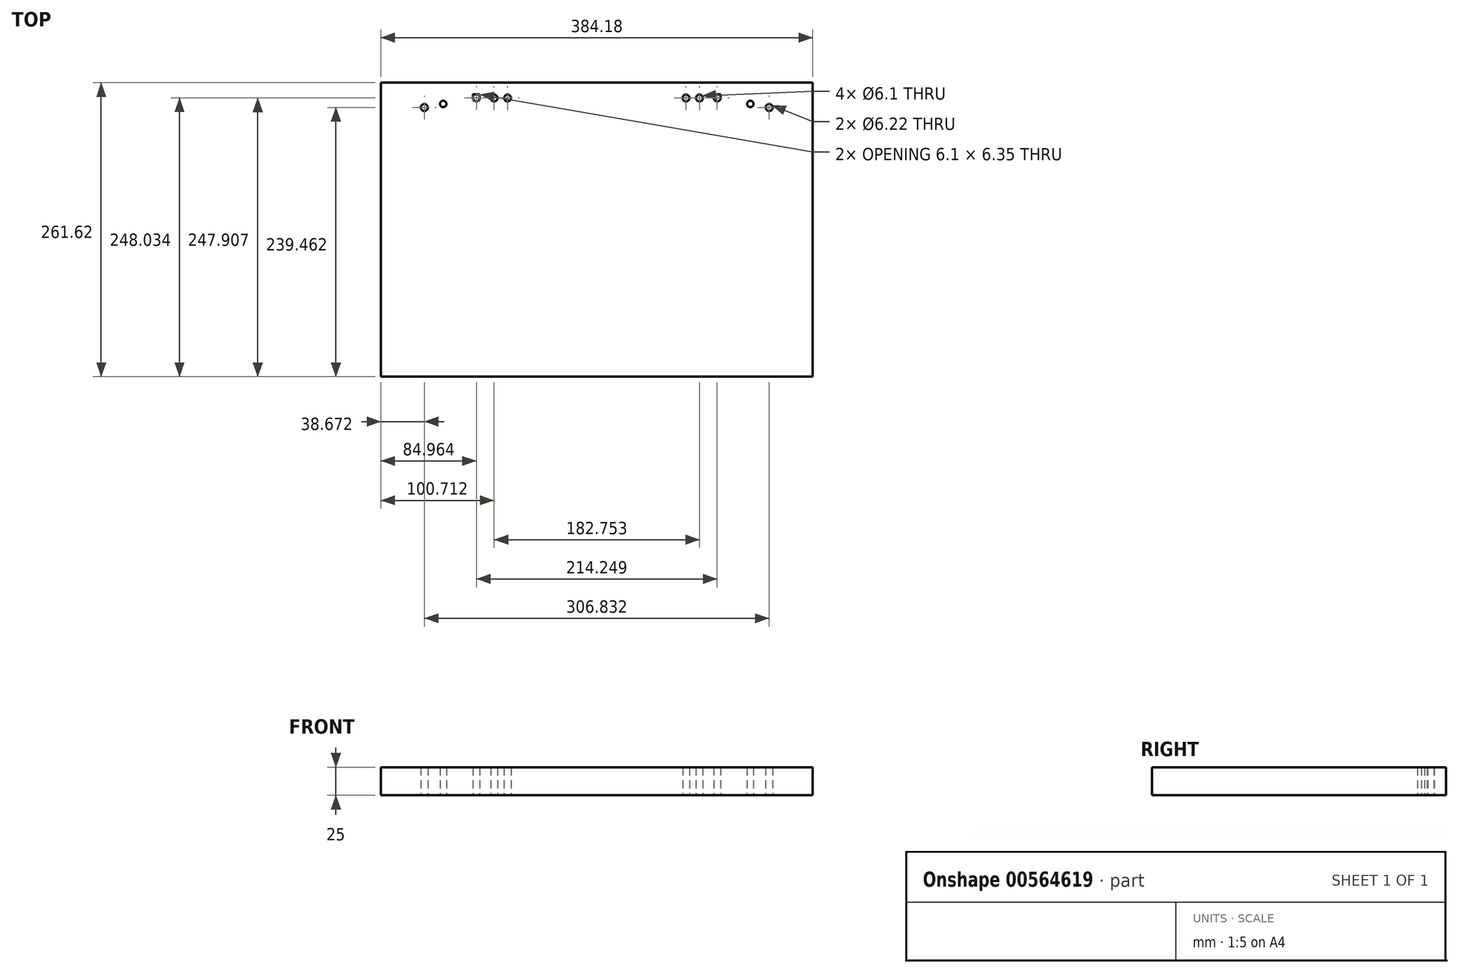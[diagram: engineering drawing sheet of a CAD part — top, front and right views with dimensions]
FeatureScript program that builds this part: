
annotation { "Feature Type Name" : "Feature", "Feature Type Description" : "" }
export const myFeature = defineFeature(function(context is Context, id is Id, definition is map)
    precondition{}
    {
        {
            var Q0;
            Q0=qCreatedBy(makeId("Top.planeOp"),FACE);
            var sketch = newSketch(context, id + "F0", { "sketchPlane" : qUnion([Q0])});
            skLineSegment(sketch, "E0.bottom", {"start": v(-193.7, 115.56) * mm, "end": v(190.47, 115.56) * mm});
            skLineSegment(sketch, "E0.top", {"start": v(-193.7, -146.06) * mm, "end": v(190.47, -146.06) * mm});
            skLineSegment(sketch, "E0.left", {"start": v(-193.7, 115.56) * mm, "end": v(-193.7, -146.06) * mm});
            skLineSegment(sketch, "E0.right", {"start": v(190.47, 115.56) * mm, "end": v(190.47, -146.06) * mm});
            skLineSegment(sketch, "E1", {"start": v(144.25, -146.06) * mm, "end": v(144.25, 88.39) * mm, "construction": true});
            skLineSegment(sketch, "E2", {"start": v(72.23, 88.39) * mm, "end": v(156.3, 88.39) * mm});
            skLineSegment(sketch, "E3", {"start": v(156.3, 88.39) * mm, "end": v(156.3, 100.96) * mm});
            skLineSegment(sketch, "E4", {"start": v(156.3, 94.67) * mm, "end": v(190.47, 94.67) * mm, "construction": true});
            skLineSegment(sketch, "E5", {"start": v(151.8, -146.06) * mm, "end": v(151.8, 90.3) * mm, "construction": true});
            skLineSegment(sketch, "E6", {"start": v(190.47, 93.4) * mm, "end": v(154.9, 93.4) * mm, "construction": true});
            skCircle(sketch, "E7", {"center": v(151.8, 93.4) * mm, "radius": 3.11 * mm});
            skLineSegment(sketch, "E8", {"start": v(151.8, 90.3) * mm, "end": v(151.8, 93.4) * mm, "construction": true});
            skLineSegment(sketch, "E9", {"start": v(154.9, 93.4) * mm, "end": v(151.8, 93.4) * mm, "construction": true});
            skLineSegment(sketch, "E10", {"start": v(135.03, -146.06) * mm, "end": v(135.03, 93.72) * mm, "construction": true});
            skLineSegment(sketch, "E11", {"start": v(190.47, 96.58) * mm, "end": v(137.89, 96.58) * mm, "construction": true});
            skCircle(sketch, "E12", {"center": v(135.03, 96.58) * mm, "radius": 2.86 * mm});
            skLineSegment(sketch, "E13", {"start": v(135.03, 96.58) * mm, "end": v(137.89, 96.58) * mm, "construction": true});
            skLineSegment(sketch, "E14", {"start": v(135.03, 96.58) * mm, "end": v(135.03, 93.72) * mm, "construction": true});
            skLineSegment(sketch, "E15", {"start": v(190.47, 101.85) * mm, "end": v(108.55, 101.85) * mm, "construction": true});
            skLineSegment(sketch, "E16", {"start": v(105.5, -146.06) * mm, "end": v(105.5, 98.8) * mm, "construction": true});
            skLineSegment(sketch, "E17", {"start": v(105.5, 101.85) * mm, "end": v(108.55, 101.85) * mm, "construction": true});
            skLineSegment(sketch, "E18", {"start": v(105.5, 101.85) * mm, "end": v(105.5, 98.8) * mm, "construction": true});
            skLineSegment(sketch, "E19", {"start": v(105.5, 101.85) * mm, "end": v(102.45, 101.85) * mm, "construction": true});
            skLineSegment(sketch, "E20", {"start": v(102.45, 101.85) * mm, "end": v(102.45, 101.85) * mm});
            skLineSegment(sketch, "E21", {"start": v(108.55, 101.85) * mm, "end": v(108.55, 101.85) * mm});
            skArc(sketch, "E22", {"start": v(102.45, 101.85) * mm, "mid": v(105.5, 98.8) * mm, "end": v(108.55, 101.85) * mm});
            skLineSegment(sketch, "E23", {"start": v(102.45, 101.85) * mm, "end": v(102.45, 105.15) * mm});
            skLineSegment(sketch, "E24", {"start": v(102.45, 105.15) * mm, "end": v(108.55, 105.15) * mm});
            skLineSegment(sketch, "E25", {"start": v(108.55, 105.15) * mm, "end": v(108.55, 101.85) * mm});
            skLineSegment(sketch, "E26", {"start": v(102.45, 101.85) * mm, "end": v(92.8, 101.85) * mm, "construction": true});
            skCircle(sketch, "E27", {"center": v(89.75, 101.85) * mm, "radius": 3.05 * mm});
            skLineSegment(sketch, "E28", {"start": v(86.7, 101.85) * mm, "end": v(80.81, 101.85) * mm, "construction": true});
            skCircle(sketch, "E29", {"center": v(77.77, 101.85) * mm, "radius": 3.05 * mm});
            skLineSegment(sketch, "E30", {"start": v(72.23, 88.39) * mm, "end": v(72.23, 107.44) * mm});
            skLineSegment(sketch, "E31", {"start": v(72.23, 107.44) * mm, "end": v(156.3, 107.44) * mm});
            skLineSegment(sketch, "E32", {"start": v(156.3, 107.44) * mm, "end": v(156.3, 100.96) * mm});
            skLineSegment(sketch, "E33", {"start": v(-1.62, 115.56) * mm, "end": v(-1.62, -146.06) * mm});
            skLineSegment(sketch, "E34.MirrorCS", {"start": v(-75.47, 107.44) * mm, "end": v(-159.55, 107.44) * mm});
            skLineSegment(sketch, "E35.MirrorCS", {"start": v(-105.7, 101.85) * mm, "end": v(-105.7, 105.15) * mm});
            skLineSegment(sketch, "E36.MirrorCS", {"start": v(-108.75, 101.85) * mm, "end": v(-111.8, 101.85) * mm, "construction": true});
            skLineSegment(sketch, "E37.MirrorCS", {"start": v(-108.75, 101.85) * mm, "end": v(-105.7, 101.85) * mm, "construction": true});
            skLineSegment(sketch, "E38.MirrorCS", {"start": v(-138.27, 96.58) * mm, "end": v(-141.13, 96.58) * mm, "construction": true});
            skLineSegment(sketch, "E39.MirrorCS", {"start": v(-108.75, 101.85) * mm, "end": v(-108.75, 98.8) * mm, "construction": true});
            skLineSegment(sketch, "E40.MirrorCS", {"start": v(-155.04, 90.3) * mm, "end": v(-155.04, 93.4) * mm, "construction": true});
            skCircle(sketch, "E41.MirrorC", {"center": v(-81, 101.85) * mm, "radius": 3.05 * mm});
            skCircle(sketch, "E42.MirrorC", {"center": v(-138.27, 96.58) * mm, "radius": 2.86 * mm});
            skLineSegment(sketch, "E43.MirrorCS", {"start": v(-159.55, 107.44) * mm, "end": v(-159.55, 100.96) * mm});
            skLineSegment(sketch, "E44.MirrorCS", {"start": v(-75.47, 88.39) * mm, "end": v(-75.47, 107.44) * mm});
            skArc(sketch, "E45.MirrorCS", {"start": v(-105.7, 101.85) * mm, "mid": v(-108.75, 98.8) * mm, "end": v(-111.8, 101.85) * mm});
            skLineSegment(sketch, "E46.MirrorCS", {"start": v(-159.55, 88.39) * mm, "end": v(-159.55, 100.96) * mm});
            skLineSegment(sketch, "E47.MirrorCS", {"start": v(-105.7, 101.85) * mm, "end": v(-105.7, 101.85) * mm});
            skLineSegment(sketch, "E48.MirrorCS", {"start": v(-158.15, 93.4) * mm, "end": v(-155.04, 93.4) * mm, "construction": true});
            skCircle(sketch, "E49.MirrorC", {"center": v(-155.04, 93.4) * mm, "radius": 3.11 * mm});
            skLineSegment(sketch, "E50.MirrorCS", {"start": v(-111.8, 105.15) * mm, "end": v(-111.8, 101.85) * mm});
            skLineSegment(sketch, "E51.MirrorCS", {"start": v(-75.47, 88.39) * mm, "end": v(-159.55, 88.39) * mm});
            skLineSegment(sketch, "E52.MirrorCS", {"start": v(-105.7, 105.15) * mm, "end": v(-111.8, 105.15) * mm});
            skLineSegment(sketch, "E53.MirrorCS", {"start": v(-111.8, 101.85) * mm, "end": v(-111.8, 101.85) * mm});
            skCircle(sketch, "E54.MirrorC", {"center": v(-93, 101.85) * mm, "radius": 3.05 * mm});
            skLineSegment(sketch, "E55.MirrorCS", {"start": v(-138.27, 96.58) * mm, "end": v(-138.27, 93.72) * mm, "construction": true});
            skSolve(sketch);
        }
        {
            var Q0;
            Q0=makeQuery(id+"F0.imprint","IMPRINT",FACE,{"disambiguationData":[TD([[makeQuery(id+"F0.imprint","IMPRINT",EDGE,{"derivedFrom":sQuery(id+"F0.wireOp",EDGE,"E2")}),1.0]])]});
            var Q1;
            Q1=makeQuery(id+"F0.imprint","IMPRINT",FACE,{"disambiguationData":[TD([[makeQuery(id+"F0.imprint","IMPRINT",EDGE,{"derivedFrom":sQuery(id+"F0.wireOp",EDGE,"E35.MirrorCS")}),-1.0]])]});
            var Q2;
            {var subQ1=sQuery(id+"F0.wireOp",EDGE,"E0.left");Q2=makeQuery(id+"F0.imprint","IMPRINT",FACE,{"disambiguationData":[TD([[makeQuery(id+"F0.imprint","IMPRINT",EDGE,{"derivedFrom":subQ1}),1.0]])]});}
            var Q3;
            {var subQ0=sQuery(id+"F0.wireOp",EDGE,"E0.right");Q3=makeQuery(id+"F0.imprint","IMPRINT",FACE,{"disambiguationData":[TD([[makeQuery(id+"F0.imprint","IMPRINT",EDGE,{"derivedFrom":subQ0}),-1.0]])]});}
            extrude(context, id + "F1", {"entities" : qUnion([Q0, Q1, Q2, Q3]), "depth" : 25 * mm, "offsetDistance" : 25 * mm});
        }
    });
